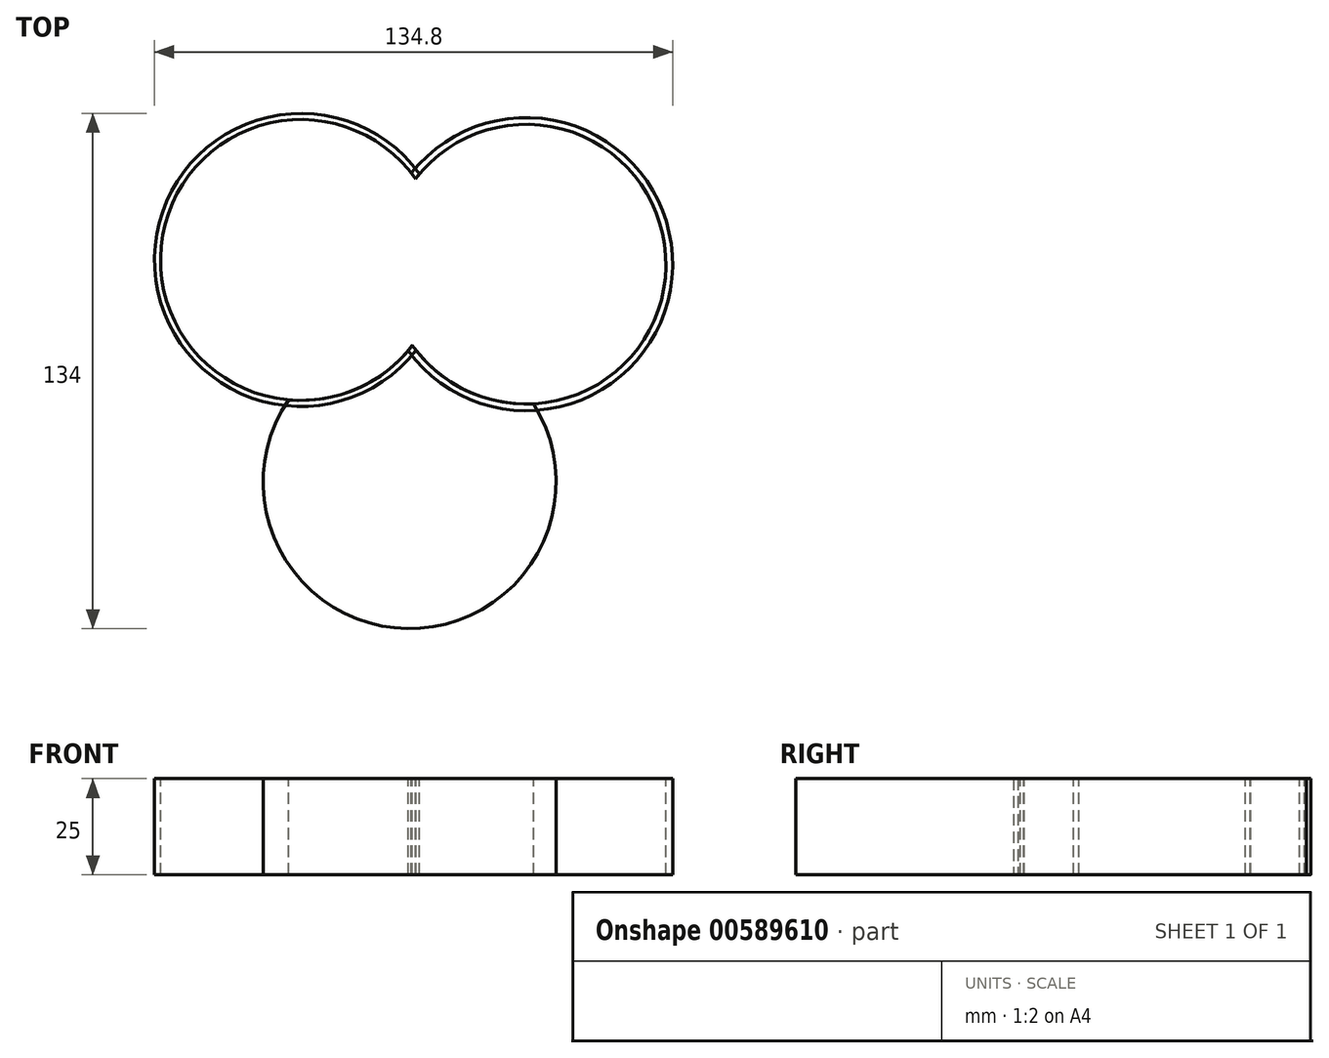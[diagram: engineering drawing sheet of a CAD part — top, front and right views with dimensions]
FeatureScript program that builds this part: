
annotation { "Feature Type Name" : "Feature", "Feature Type Description" : "" }
export const myFeature = defineFeature(function(context is Context, id is Id, definition is map)
    precondition{}
    {
        {
            var Q0;
            Q0=qCreatedBy(makeId("Top.planeOp"),FACE);
            var sketch = newSketch(context, id + "F0", { "sketchPlane" : qUnion([Q0])});
            skCircle(sketch, "E0", {"center": v(-28.64, 28.64) * mm, "radius": 38.1 * mm});
            skSolve(sketch);
        }
        {
            var Q0;
            Q0=makeQuery(id+"F0.imprint","IMPRINT",FACE,{"disambiguationData":[TD([[makeQuery(id+"F0.imprint","IMPRINT",EDGE,{"derivedFrom":sQuery(id+"F0.wireOp",EDGE,"E0")}),1.0]])]});
            extrude(context, id + "F1", {"entities" : qUnion([Q0]), "depth" : 25 * mm, "offsetDistance" : 25 * mm});
        }
        {
            var Q0;
            Q0=makeQuery(id+"F1.opExtrude","SWEPT_BODY",BODY,{"disambiguationData":[OSD([sQuery(id+"F0.wireOp",EDGE,"E0")])]});
            transform(context, id + "F2", {"entities" : qUnion([Q0]), "transformType" : TransformType.TRANSLATION_3D, "dx" : 58.6 * mm, "dy" : -1.1 * mm, "dz" : 0 * mm, "makeCopy" : true});
        }
        {
            var Q0;
            Q0=makeQuery(id+"F1.opExtrude","SWEPT_BODY",BODY,{"disambiguationData":[OSD([sQuery(id+"F0.wireOp",EDGE,"E0")])]});
            transform(context, id + "F3", {"entities" : qUnion([Q0]), "transformType" : TransformType.TRANSLATION_3D, "dx" : 28.3 * mm, "dy" : -57.8 * mm, "dz" : 0 * mm, "makeCopy" : true});
        }
        {
            var Q0;
            Q0=makeQuery(id+"F3.opPattern","COPY",FACE,{"derivedFrom":makeQuery(id+"F1.opExtrude","CAP_FACE",FACE,{"disambiguationData":[OSD([sQuery(id+"F0.wireOp",EDGE,"E0")])],"isStart":false}),"instanceName":"1"});
            var sketch = newSketch(context, id + "F4", { "sketchPlane" : qUnion([Q0])});
            skSolve(sketch);
        }
        {
            var Q0;
            Q0=makeQuery(id+"F1.opExtrude","CAP_FACE",FACE,{"disambiguationData":[OSD([sQuery(id+"F0.wireOp",EDGE,"E0")])],"isStart":false});
            var sketch = newSketch(context, id + "F5", { "sketchPlane" : qUnion([Q0])});
            skCircle(sketch, "E1", {"center": v(-28.64, 28.64) * mm, "radius": 36.54 * mm});
            skSolve(sketch);
        }
        {
            var Q0;
            Q0=makeQuery(id+"F2.opPattern","COPY",FACE,{"derivedFrom":makeQuery(id+"F1.opExtrude","CAP_FACE",FACE,{"disambiguationData":[OSD([sQuery(id+"F0.wireOp",EDGE,"E0")])],"isStart":false}),"instanceName":"1"});
            var sketch = newSketch(context, id + "F6", { "sketchPlane" : qUnion([Q0])});
            skCircle(sketch, "E2", {"center": v(29.96, 27.54) * mm, "radius": 36.38 * mm});
            skSolve(sketch);
        }
        {
            var Q0;
            Q0 = qSketchRegion(id + "F5", true);
            extrude(context, id + "F7", {"entities" : qUnion([Q0]), "operationType" : NewBodyOperationType.REMOVE, "oppositeDirection" : true, "depth" : 25 * mm, "offsetDistance" : 25 * mm});
        }
        {
            var Q0;
            Q0=makeQuery(id+"F6.imprint","IMPRINT",FACE,{"disambiguationData":[TD([[makeQuery(id+"F6.imprint","IMPRINT",EDGE,{"derivedFrom":sQuery(id+"F6.wireOp",EDGE,"E2")}),1.0]])]});
            extrude(context, id + "F8", {"entities" : qUnion([Q0]), "operationType" : NewBodyOperationType.REMOVE, "oppositeDirection" : true, "depth" : 100 * mm, "offsetDistance" : 25 * mm});
        }
    });
